# Revit family: pdfy-p22_140gmg9_60Hz
name_source: partatom
category: 機械設備
units: mm (PartAtom-declared; Revit-internal decimal feet)

## family parameters
OmniClass タイトル = Split System Air Conditioning Units
OmniClass 番号 = 23.75.10.24.21.27.27
パーツ タイプ = 標準
ロード時にボイドで切り取り = いいえ
丸型コネクタ寸法 = 直径を使用
作業面ベース = いいえ
共有 = いいえ
常に垂直 = いいえ
部屋計算ポイント = はい

## types (10) — shared parameters
Depth = 701  [stored 2.29987 ft]
Height = 250  [stored 0.82021 ft]
IfcExportAs = IfcUnitaryEquipmentType
IfcExportType = AIRCONDITIONINGUNIT
OmniClassCode = 23-33 17 13 11
URL = https://www.mitsubishielectric.co.jp
Uniclass2015Code = Pr_70_65_03_84
Uniclass2015Title = Split coil remote air cooled condensing units
Uniclass2015Version = Systems v1.9
ダクト高 = 178 mm
ドレン管径 = 32.00 mm
パネル マテリアル = <カテゴリ別>
仕様書バージョン = Version1.0
企業コード = 108420
冷媒管径 = 100.00 mm
冷媒高低圧ガス管径 = 0.00 mm
分類コード = 50053003221050
加湿給水管径 = 0.00 mm
参照している仕様書等のバージョン = 公共建築工事標準仕様書（機械設備工事編）平成31年度版
周波数 = 60 Hz
呼称 = 室内機_天井吊(隠ぺい)形(?ダクト形)
始動方式 = 直入
形式 = 天井吊（隠ぺい）形（片ダクト形）
極数 = 1
機外静圧 = 30.0 Pa
法定耐用年数 = 15
消費電力_加湿器 = 0 W
消費電力_電気ヒーター = 0 W
相 = 1
相_電気ヒーター = 1
積算_科目 = 1 空気調和設備
符号 = ACP-CIS
製品リリース年月 = 2022年9月15日
製品出荷対象 = 国内
製造元 = 三菱電機株式会社
設置方法 = 天井吊(隠ぺい)形
説明 = ビル用マルチエアコン 室内ユニット 天井ビルトイン形
負荷分類 = 10_ファンコイル類
運転質量 = 0.00 kg
電圧 = 200 V
電圧_電気ヒーター = 0 V
zero-valued in all types: 価格, 有効加湿量

## per-type parameters (varying)
| type | MAX風量 | MID風量 | MIN風量 | Width | ダクト幅 | 冷媒ガス管径 | 冷媒液管径 | 冷媒管径符号 | 冷房能力 | 暖房能力 | 消費電力 | 消費電力_冷房 | 消費電力_暖房 | 製品質量 | 質量 | 電動機出力_送風機 | 音響パワーレベル(dB) | 風量 | 風量（m3／min） | 風量（中）（m3／min） | 風量（弱）（m3／min） | 騒音レベル（中）(dB) | 騒音レベル（弱）(dB) |
| PDFY-P22GMG9 | 510.0 m³/h | 450.0 m³/h | 360.0 m³/h | 700  [stored 2.29659 ft] | 660 mm | 12.70 mm | 6.35 mm | Ac | 2 kW | 3 kW | 90 W | 90 W | 70 W | 24.00 kg | 28.80 kg | 85 W | 57 | 510.0 m³/h | 8.5 | 7.5 | 6 | 55 | 51 |
| PDFY-P28GMG9 | 510.0 m³/h | 450.0 m³/h | 360.0 m³/h | 700  [stored 2.29659 ft] | 660 mm | 12.70 mm | 6.35 mm | Ac | 3 kW | 3 kW | 90 W | 90 W | 70 W | 24.00 kg | 28.80 kg | 85 W | 57 | 510.0 m³/h | 8.5 | 7.5 | 6 | 56 | 51 |
| PDFY-P36GMG9 | 630.0 m³/h | 540.0 m³/h | 420.0 m³/h | 700  [stored 2.29659 ft] | 660 mm | 12.70 mm | 6.35 mm | Ac | 4 kW | 4 kW | 130 W | 130 W | 110 W | 24.00 kg | 28.80 kg | 85 W | 61 | 630.0 m³/h | 10.5 | 9 | 7 | 58 | 53 |
| PDFY-P45GMG9 | 840.0 m³/h | 720.0 m³/h | 540.0 m³/h | 900  [stored 2.95276 ft] | 860 mm | 12.70 mm | 6.35 mm | Ac | 5 kW | 5 kW | 140 W | 140 W | 120 W | 28.00 kg | 33.60 kg | 85 W | 59 | 840.0 m³/h | 14 | 12 | 9 | 56 | 53 |
| PDFY-P56GMG9 | 1020.0 m³/h | 870.0 m³/h | 600.0 m³/h | 900  [stored 2.95276 ft] | 860 mm | 15.90 mm | 6.35 mm | Ac | 6 kW | 6 kW | 150 W | 150 W | 130 W | 28.00 kg | 33.60 kg | 85 W | 62 | 1020.0 m³/h | 17 | 14.5 | 10 | 60 | 54 |
| PDFY-P71GMG9 | 1140.0 m³/h | 960.0 m³/h | 750.0 m³/h | 1100 | 1060 mm | 15.90 mm | 9.52 mm | Bd | 7 kW | 8 kW | 160 W | 160 W | 140 W | 33.00 kg | 39.60 kg | 121 W | 63 | 1140.0 m³/h | 19 | 16 | 12.5 | 60 | 56 |
| PDFY-P80GMG9 | 1320.0 m³/h | 1080.0 m³/h | 780.0 m³/h | 1100 | 1060 mm | 15.90 mm | 9.52 mm | Bd | 8 kW | 9 kW | 190 W | 190 W | 170 W | 33.00 kg | 39.60 kg | 121 W | 64 | 1320.0 m³/h | 22 | 18 | 13 | 61 | 57 |
| PDFY-P90GMG9 | 1320.0 m³/h | 1080.0 m³/h | 780.0 m³/h | 1100 | 1060 mm | 15.90 mm | 9.52 mm | Bd | 9 kW | 10 kW | 190 W | 190 W | 170 W | 33.00 kg | 39.60 kg | 121 W | 64 | 1320.0 m³/h | 22 | 18 | 13 | 61 | 58 |
| PDFY-P112GMG9 | 1980.0 m³/h | 1680.0 m³/h | 1200.0 m³/h | 1400  [stored 4.59318 ft] | 1360 mm | 15.90 mm | 9.52 mm | Bd | 11 kW | 13 kW | 300 W | 300 W | 280 W | 42.00 kg | 50.40 kg | 244 W | 67 | 1980.0 m³/h | 33 | 28 | 20 | 63 | 59 |
| PDFY-P140GMG9 | 2400.0 m³/h | 2040.0 m³/h | 1440.0 m³/h | 1400  [stored 4.59318 ft] | 1360 mm | 15.90 mm | 9.52 mm | Bd | 14 kW | 16 kW | 410 W | 410 W | 390 W | 42.00 kg | 50.40 kg | 244 W | 70 | 2400.0 m³/h | 40 | 34 | 24 | 67 | 62 |

note: column(s) folded — value = type name in every type: モデル

note: [stored X ft] marks values corroborated as IEEE doubles in the binary element streams (Revit-internal decimal feet)
